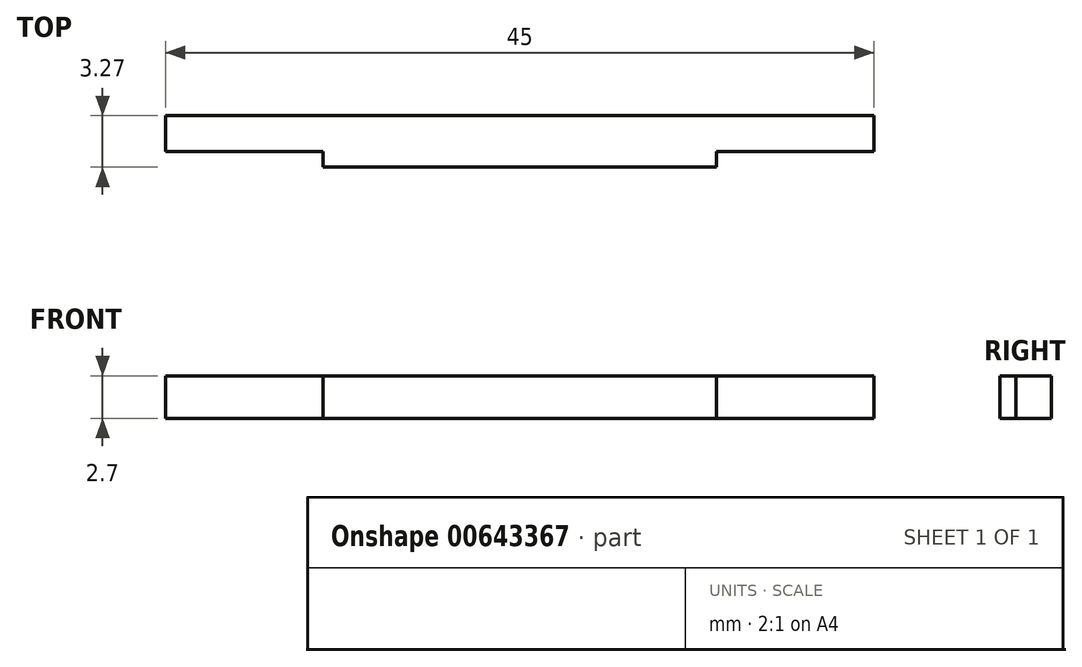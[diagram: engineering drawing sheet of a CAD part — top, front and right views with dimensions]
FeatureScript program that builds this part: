
annotation { "Feature Type Name" : "Feature", "Feature Type Description" : "" }
export const myFeature = defineFeature(function(context is Context, id is Id, definition is map)
    precondition{}
    {
        {
            var Q0;
            Q0=qCreatedBy(makeId("Right.planeOp"),FACE);
            var sketch = newSketch(context, id + "F0", { "sketchPlane" : qUnion([Q0])});
            skLineSegment(sketch, "E0.bottom", {"start": v(0, 0) * mm, "end": v(3.27, 0) * mm});
            skLineSegment(sketch, "E0.top", {"start": v(0, 2.7) * mm, "end": v(3.27, 2.7) * mm});
            skLineSegment(sketch, "E0.left", {"start": v(0, 0) * mm, "end": v(0, 2.7) * mm});
            skLineSegment(sketch, "E0.right", {"start": v(3.27, 0) * mm, "end": v(3.27, 2.7) * mm});
            skSolve(sketch);
        }
        {
            var Q0;
            Q0=makeQuery(id+"F0.imprint","IMPRINT",FACE,{"disambiguationData":[TD([[makeQuery(id+"F0.imprint","IMPRINT",EDGE,{"derivedFrom":sQuery(id+"F0.wireOp",EDGE,"E0.bottom")}),1.0]])]});
            extrude(context, id + "F1", {"entities" : qUnion([Q0]), "depth" : 45 * mm, "offsetDistance" : 25 * mm});
        }
        {
            var Q0;
            Q0=makeQuery(id+"F1.opExtrude","SWEPT_FACE",FACE,{"disambiguationData":[OSD([sQuery(id+"F0.wireOp",EDGE,"E0.left")])]});
            var sketch = newSketch(context, id + "F2", { "sketchPlane" : qUnion([Q0])});
            skLineSegment(sketch, "E1.bottom", {"start": v(45, 2.7) * mm, "end": v(35, 2.7) * mm});
            skLineSegment(sketch, "E1.top", {"start": v(45, 0) * mm, "end": v(35, 0) * mm});
            skLineSegment(sketch, "E1.left", {"start": v(45, 2.7) * mm, "end": v(45, 0) * mm});
            skLineSegment(sketch, "E1.right", {"start": v(35, 2.7) * mm, "end": v(35, 0) * mm});
            skLineSegment(sketch, "E2.bottom", {"start": v(0, 2.7) * mm, "end": v(10, 2.7) * mm});
            skLineSegment(sketch, "E2.top", {"start": v(0, 0) * mm, "end": v(10, 0) * mm});
            skLineSegment(sketch, "E2.left", {"start": v(0, 2.7) * mm, "end": v(0, 0) * mm});
            skLineSegment(sketch, "E2.right", {"start": v(10, 2.7) * mm, "end": v(10, 0) * mm});
            skSolve(sketch);
        }
        {
            var Q0;
            Q0=makeQuery(id+"F2.imprint","IMPRINT",FACE,{"disambiguationData":[TD([[makeQuery(id+"F2.imprint","IMPRINT",EDGE,{"derivedFrom":sQuery(id+"F2.wireOp",EDGE,"E1.bottom")}),1.0]])]});
            var Q1;
            Q1=makeQuery(id+"F2.imprint","IMPRINT",FACE,{"disambiguationData":[TD([[makeQuery(id+"F2.imprint","IMPRINT",EDGE,{"derivedFrom":sQuery(id+"F2.wireOp",EDGE,"E2.bottom")}),1.0]])]});
            extrude(context, id + "F3", {"entities" : qUnion([Q0, Q1]), "operationType" : NewBodyOperationType.REMOVE, "oppositeDirection" : true, "depth" : 1 * mm, "offsetDistance" : 25 * mm});
        }
    });
